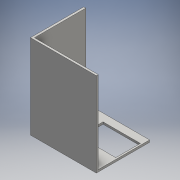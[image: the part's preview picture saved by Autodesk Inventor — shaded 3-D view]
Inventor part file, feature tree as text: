
AUTODESK INVENTOR PART (.ipt)
format: ipt  version: 2016 (Build 200138000, 138)  size: 115,712 bytes
history: native  units: mm
features: extrude x3, sketch x3
ambient origin geometry x8: Origin, YZ Plane, XZ Plane, XY Plane, X Axis, Y Axis, Z Axis, Center Point
bodies: 实体1 (feature_tree)
feature tree (6):
  extrude  "拉伸1"  Depth=2525.0mm
  extrude  "拉伸2"  Depth=75.0mm
  extrude  "拉伸3"  Depth=1170.0mm
  sketch  "草图1"  dims[d0=3125.0mm d1=2525.0mm]
  sketch  "草图3"  dims[d2=360.0mm d3=75.0mm]
  sketch  "草图4"  dims[d4=1770.0mm d5=1170.0mm d6=100.0mm d7=0.0mm d10=3900.0mm d11=0.0mm d14=3900.0mm d15=0.0mm d16=100.0mm]
